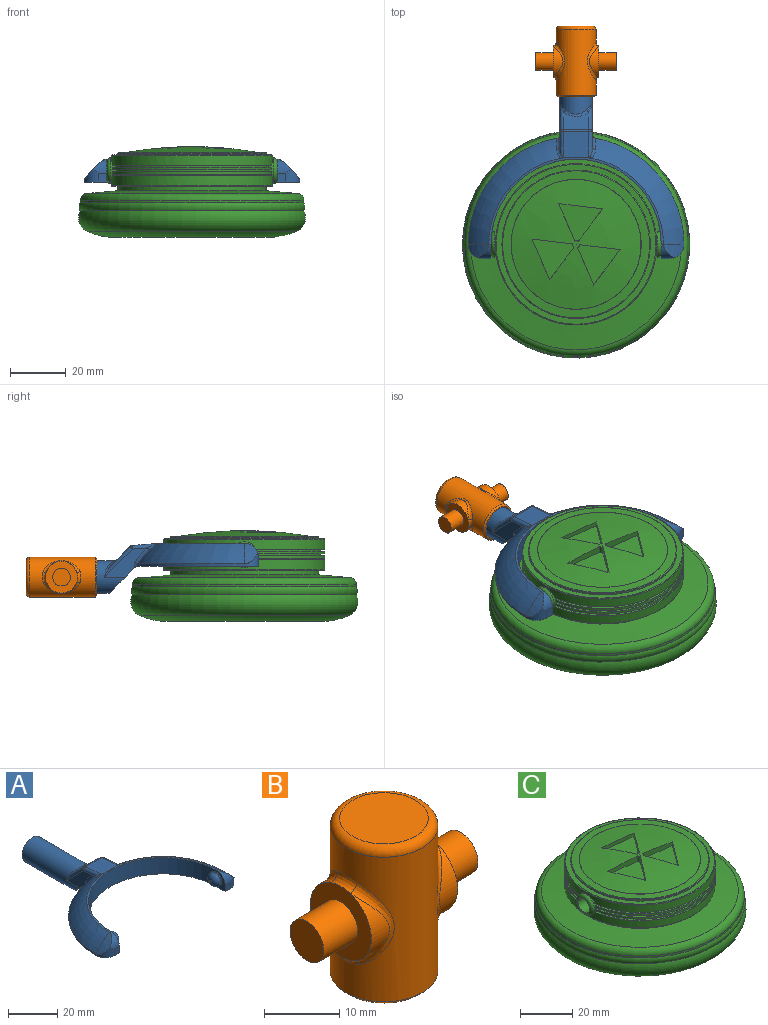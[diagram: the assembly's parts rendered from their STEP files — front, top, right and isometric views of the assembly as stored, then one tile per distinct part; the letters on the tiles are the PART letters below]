
ASSEMBLY  parts=3 mates=2
PART A: 48 faces, bbox 77.3x80.8x18.2 mm
  f0: plane 11.99x9.83mm, normal (0,-0.71,-0.71), area 141.5mm2, adj f1,f2,f9,f30,f43,f46
  f1: plane 15.39x10.49mm, normal (-1,0,0), area 63.5mm2, adj f0,f30,f32,f36,f46,f47
  f2: plane 15.39x10.49mm, normal (1,0,0), area 63.5mm2, adj f0,f30,f34,f39,f43,f44
  f3: plane 9.14x6.37mm, normal (0,0.71,0.71), area 67.6mm2, adj f35,f36,f39,f40
  f4: cylinder r=38.61mm len=37.99mm, axis (0,0,-1), area 42.6mm2, adj f6,f9,f17,f46,f47
  f5: torus R=19.3mm, axis (0,0,-1), area 507.8mm2, adj f10,f11,f12,f29,f42,f44
  f6: torus R=19.3mm, axis (0,0,-1), area 507.8mm2, adj f4,f11,f15,f28,f45,f47
  f7: cylinder r=30.48mm len=60.96mm, axis (0,0,-1), area 746.6mm2, adj f8,f9,f11,f14,f21,f24
  f8: plane 8.13x5.08mm, normal (-1,0,0), area 19.9mm2, adj f7,f9,f13,f19,f24
  f9: plane 77.22x43.73mm, normal (0,0,-1), area 956.2mm2, adj f0,f4,f7,f8,f10,f13,f14,f16
  f10: cylinder r=38.61mm len=37.99mm, axis (0,0,-1), area 42.6mm2, adj f5,f9,f20,f43,f44
  f11: plane 62.55x30.95mm, normal (0,0,1), area 75mm2, adj f5,f6,f7,f18,f19,f27
  f12: cylinder r=22.71mm len=7.33mm, axis (0,1,0), area 24.8mm2, adj f5,f19,f20
  f13: plane 3.05x3.05mm, normal (0,-1,0), area 9.3mm2, adj f8,f9,f19,f20
  f14: plane 8.13x5.08mm, normal (1,0,0), area 19.9mm2, adj f7,f9,f16,f18,f21
  f15: cylinder r=22.71mm len=7.33mm, axis (0,1,0), area 24.8mm2, adj f6,f17,f18
  f16: plane 3.05x3.05mm, normal (0,-1,0), area 9.3mm2, adj f9,f14,f17,f18
  f17: cylinder r=5.08mm len=5.08mm, axis (0,0,-1), area 21.9mm2, adj f4,f9,f15,f16,f18
  f18: cylinder r=5.08mm len=5.08mm, axis (-1,0,0), area 21.9mm2, adj f11,f14,f15,f16,f17
  f19: cylinder r=5.08mm len=5.08mm, axis (-1,0,0), area 21.9mm2, adj f8,f11,f12,f13,f20
  f20: cylinder r=5.08mm len=5.08mm, axis (0,0,-1), area 21.9mm2, adj f9,f10,f12,f13,f19
  f21: cylinder r=3.17mm len=6.35mm, axis (-1,0,0), area 12.7mm2, adj f7,f14,f23
  f22: plane 1.27x1.27mm, normal (1,0,0), area 1.3mm2, adj f23
  f23: torus R=0.64mm, axis (1,0,0), area 56.5mm2, adj f21,f22
  f24: cylinder r=3.17mm len=6.35mm, axis (1,0,0), area 12.7mm2, adj f7,f8,f26
  f25: plane 1.27x1.27mm, normal (-1,0,0), area 1.3mm2, adj f26
  f26: torus R=0.64mm, axis (-1,0,0), area 56.5mm2, adj f24,f25
  f27: plane 9.86x9.36mm, normal (0,0.09,1), area 85.6mm2, adj f11,f28,f29,f32,f34,f35,f42,f45
  f28: plane 1.04x0.17mm, normal (0,-1,0), area 0mm2, adj f6,f27,f45
  f29: plane 1.04x0.17mm, normal (0,-1,0), area 0mm2, adj f5,f27,f42
  f30: cylinder r=5.84mm len=33.01mm, axis (0,-1,0), area 1029.7mm2, adj f0,f1,f2,f31,f38,f40,f41
  f31: plane 11.68x11.68mm, normal (0,1,0), area 107.2mm2, adj f30
  f32: cylinder r=1.27mm len=9.13mm, axis (0,-1,0.09), area 14.4mm2, adj f1,f27,f33,f45
  f33: sphere r=1.27mm, area 1.5mm2, adj f32,f35,f36
  f34: cylinder r=1.27mm len=9.13mm, axis (0,1,-0.09), area 14.4mm2, adj f2,f27,f37,f42
  f35: cylinder r=1.27mm len=9.14mm, axis (-1,0,0), area 8.1mm2, adj f3,f27,f33,f37
  f36: cylinder r=1.27mm len=10.91mm, axis (0,-0.71,0.71), area 23.1mm2, adj f1,f3,f33,f38
  f37: sphere r=1.27mm, area 1.5mm2, adj f34,f35,f39
  f38: bspline ~4.55x2.75mm, area 2.3mm2, adj f30,f36,f40
  f39: cylinder r=1.27mm len=10.91mm, axis (0,0.71,-0.71), area 23.1mm2, adj f2,f3,f37,f41
  f40: bspline ~9.14x2.56mm, area 10.7mm2, adj f3,f30,f38,f41
  f41: bspline ~5.23x3.53mm, area 2.3mm2, adj f30,f39,f40
  f42: bspline ~4.62x3.14mm, area 5.2mm2, adj f5,f27,f29,f34,f44
  f43: cylinder r=1.27mm len=1.74mm, axis (0,0,-1), area 1.9mm2, adj f0,f2,f9,f10,f44
  f44: bspline ~8.6x7.86mm, area 11.9mm2, adj f2,f5,f10,f42,f43
  f45: bspline ~4.62x3.14mm, area 5.2mm2, adj f6,f27,f28,f32,f47
  f46: cylinder r=1.27mm len=1.74mm, axis (0,0,-1), area 1.9mm2, adj f0,f1,f4,f9,f47
  f47: bspline ~8.6x7.86mm, area 11.9mm2, adj f1,f4,f6,f45,f46
PART B: 25 faces, bbox 28.9x15.5x25.4 mm
  f0: cylinder r=5.71mm len=10.81mm, axis (-1,0,0), area 26.2mm2, adj f5,f15
  f1: cylinder r=5.71mm len=10.81mm, axis (-1,0,0), area 26.2mm2, adj f8,f11
  f2: cylinder r=7.14mm len=23.5mm, axis (0,0,-1), area 763.2mm2, adj f9,f10,f11,f12,f13,f14,f15,f16
  f3: plane 11.75x11.75mm, normal (0,0,1), area 108.4mm2, adj f17
  f4: plane 13.02x13.02mm, normal (0,0,-1), area 16.3mm2, adj f22,f24
  f5: plane 11.46x11.46mm, normal (1,0,0), area 70.9mm2, adj f0,f6,f13,f16,f18
  f6: cylinder r=5.71mm len=10.81mm, axis (-1,0,0), area 26.2mm2, adj f5,f14
  f7: cylinder r=5.71mm len=10.81mm, axis (-1,0,0), area 26.2mm2, adj f8,f10
  f8: plane 11.46x11.46mm, normal (-1,0,0), area 70.9mm2, adj f1,f7,f9,f12,f20
  f9: bspline ~4.64x1.73mm, area 6.5mm2, adj f2,f8,f10,f11
  f10: bspline ~13.62x4.91mm, area 20.7mm2, adj f2,f7,f9,f12
  f11: bspline ~13.6x4.87mm, area 20.7mm2, adj f1,f2,f9,f12
  f12: bspline ~4.64x1.73mm, area 6.5mm2, adj f2,f8,f10,f11
  f13: bspline ~4.64x1.73mm, area 6.5mm2, adj f2,f5,f14,f15
  f14: bspline ~13.62x4.91mm, area 20.7mm2, adj f2,f6,f13,f16
  f15: bspline ~13.6x4.87mm, area 20.7mm2, adj f0,f2,f13,f16
  f16: bspline ~4.64x1.73mm, area 6.5mm2, adj f2,f5,f14,f15
  f17: torus R=5.87mm, axis (0,0,1), area 83.8mm2, adj f2,f3
  f18: cylinder r=3.17mm len=6.35mm, axis (-1,0,0), area 126.7mm2, adj f5,f19
  f19: plane 6.35x6.35mm, normal (1,0,0), area 31.7mm2, adj f18
  f20: cylinder r=3.17mm len=6.35mm, axis (1,0,0), area 126.7mm2, adj f8,f21
  f21: plane 6.35x6.35mm, normal (-1,0,0), area 31.7mm2, adj f20
  f22: cylinder r=6.1mm len=22.86mm, axis (0,0,-1), area 875.6mm2, adj f4,f23
  f23: plane 12.19x12.19mm, normal (0,0,-1), area 116.7mm2, adj f22
  f24: cone r=7.14mm half-angle=45deg, axis (0,0,1), area 38.5mm2, adj f2,f4
PART C: 64 faces, bbox 96.3x96.3x32.5 mm
  f0: cylinder r=28.87mm len=57.73mm, axis (0,0,-1), area 628.4mm2, adj f1,f2,f54,f55,f60
  f1: plane 57.14x24.71mm, normal (0,0,1), area 101.4mm2, adj f0,f3,f54,f55
  f2: plane 57.14x24.71mm, normal (0,0,1), area 101.4mm2, adj f0,f4,f54,f55
  f3: cylinder r=27.61mm len=54.58mm, axis (0,0,-1), area 50.1mm2, adj f1,f6,f54,f55
  f4: cylinder r=27.61mm len=54.58mm, axis (0,0,-1), area 50.1mm2, adj f2,f5,f54,f55
  f5: plane 57.17x24.53mm, normal (0,0,-1), area 100.8mm2, adj f4,f8,f54,f55
  f6: plane 57.17x24.53mm, normal (0,0,-1), area 100.8mm2, adj f3,f7,f54,f55
  f7: cylinder r=28.87mm len=57.06mm, axis (0,0,-1), area 76.2mm2, adj f6,f9,f54,f55
  f8: cylinder r=28.87mm len=57.06mm, axis (0,0,-1), area 76.2mm2, adj f5,f10,f54,f55
  f9: plane 57.02x24.31mm, normal (0,0,1), area 100.4mm2, adj f7,f11,f54,f55
  f10: plane 57.02x24.31mm, normal (0,0,1), area 100.4mm2, adj f8,f12,f54,f55
  f11: cylinder r=27.61mm len=54.45mm, axis (0,0,-1), area 48.1mm2, adj f9,f13,f54,f55
  f12: cylinder r=27.61mm len=54.45mm, axis (0,0,-1), area 48.1mm2, adj f10,f14,f54,f55
  f13: plane 57.12x24.36mm, normal (0,0,-1), area 100.4mm2, adj f11,f15,f54,f55
  f14: plane 57.12x24.36mm, normal (0,0,-1), area 100.4mm2, adj f12,f16,f54,f55
  f15: cylinder r=28.87mm len=57.06mm, axis (0,0,-1), area 79.3mm2, adj f13,f22,f54,f55
  f16: cylinder r=28.87mm len=57.06mm, axis (0,0,-1), area 79.3mm2, adj f14,f21,f54,f55
  f17: cylinder r=27.61mm len=54.58mm, axis (0,0,-1), area 50.1mm2, adj f19,f22,f54,f55
  f18: cylinder r=27.61mm len=54.58mm, axis (0,0,-1), area 50.1mm2, adj f20,f21,f54,f55
  f19: plane 57.24x24.77mm, normal (0,0,-1), area 101.4mm2, adj f17,f23,f54,f55
  f20: plane 57.24x24.77mm, normal (0,0,-1), area 101.4mm2, adj f18,f23,f54,f55
  f21: plane 57.07x24.48mm, normal (0,0,1), area 100.8mm2, adj f16,f18,f54,f55
  f22: plane 57.07x24.48mm, normal (0,0,1), area 100.8mm2, adj f15,f17,f54,f55
  f23: cylinder r=28.87mm len=57.73mm, axis (0,0,-1), area 595.8mm2, adj f19,f20,f54,f55,f61
  f24: sphere r=135.39mm, area 1385.3mm2, adj f38,f39,f40,f41,f43,f44,f45,f46
  f25: plane 39.33x39.33mm, normal (0,0,-1), area 1214.6mm2, adj f26
  f26: torus R=20.12mm, axis (0,0,-1), area 1429.3mm2, adj f25,f27
  f27: torus R=27.74mm, axis (0,0,-1), area 3542.1mm2, adj f26,f28
  f28: torus R=35.36mm, axis (0,0,-1), area 2180.1mm2, adj f27,f29
  f29: torus R=37.64mm, axis (0,0,-1), area 740.9mm2, adj f28,f30
  f30: cylinder r=40.06mm len=80.11mm, axis (0,0,-1), area 213.3mm2, adj f29,f34
  f31: cone r=26.57mm half-angle=85deg, axis (0,0,-1), area 2265mm2, adj f32,f34
  f32: cylinder r=26.57mm len=53.14mm, axis (0,0,-1), area 265mm2, adj f31,f33
  f33: plane 57.23x57.23mm, normal (0,0,-1), area 354.5mm2, adj f32,f60
  f34: torus R=37.52mm, axis (0,0,1), area 928.6mm2, adj f30,f31
  f35: cone r=26.57mm half-angle=87deg, axis (0,0,-1), area 475.4mm2, adj f62,f63
  f36: cylinder r=26.57mm len=53.14mm, axis (0,0,-1), area 92.3mm2, adj f37,f62
  f37: plane 57.23x57.23mm, normal (0,0,1), area 354.5mm2, adj f36,f61
  f38: plane 13.42x5.76mm, normal (0.92,0.39,0), area 32.2mm2, adj f24,f39,f41,f42
  f39: cylinder r=1.27mm len=2.53mm, axis (0,0,1), area 3.4mm2, adj f24,f38,f40,f42
  f40: plane 11.7x8.74mm, normal (-0.8,0.6,0), area 32.2mm2, adj f24,f39,f41,f42
  f41: plane 15.76x1.87mm, normal (-0.12,-0.99,0), area 28mm2, adj f24,f38,f40,f42
  f42: plane 15.76x13.57mm, normal (0,0,1), area 108.3mm2, adj f38,f39,f40,f41
  f43: plane 14.5x2.53mm, normal (-0.12,-0.99,0), area 32.2mm2, adj f24,f44,f46,f47
  f44: cylinder r=1.27mm len=2.53mm, axis (0,0,1), area 3.4mm2, adj f24,f43,f45,f47
  f45: plane 13.42x5.76mm, normal (0.92,0.39,0), area 32.2mm2, adj f24,f44,f46,f47
  f46: plane 12.72x9.5mm, normal (-0.8,0.6,0), area 28mm2, adj f24,f43,f45,f47
  f47: plane 15.26x14.44mm, normal (0,0,1), area 108.3mm2, adj f43,f44,f45,f46
  f48: cylinder r=1.27mm len=2.53mm, axis (0,0,1), area 3.4mm2, adj f24,f49,f51,f52
  f49: plane 14.5x2.53mm, normal (-0.12,-0.99,0), area 32.2mm2, adj f24,f48,f50,f52
  f50: plane 14.59x6.26mm, normal (0.92,0.39,0), area 28mm2, adj f24,f49,f51,f52
  f51: plane 11.7x8.74mm, normal (-0.8,0.6,0), area 32.2mm2, adj f24,f48,f50,f52
  f52: plane 15x14.59mm, normal (0,0,1), area 108.3mm2, adj f48,f49,f50,f51
  f53: plane 6.6x6.6mm, normal (1,0,0), area 2.6mm2, adj f58,f59
  f54: cylinder r=4.57mm len=9.14mm, axis (-1,0,0), area 23.9mm2, adj f0,f1,f2,f3,f4,f5,f6,f7
  f55: cylinder r=4.57mm len=9.14mm, axis (-1,0,0), area 22.3mm2, adj f0,f1,f2,f3,f4,f5,f6,f7
  f56: plane 6.6x6.6mm, normal (-1,0,0), area 2.6mm2, adj f57,f59
  f57: torus R=3.3mm, axis (1,0,0), area 51.5mm2, adj f55,f56
  f58: torus R=3.3mm, axis (1,0,0), area 51.5mm2, adj f53,f54
  f59: cylinder r=3.17mm len=60.96mm, axis (1,0,0), area 1216.1mm2, adj f53,f56
  f60: torus R=28.61mm, axis (0,0,1), area 72.1mm2, adj f0,f33
  f61: torus R=28.61mm, axis (0,0,-1), area 72.1mm2, adj f23,f37
  f62: torus R=26.31mm, axis (0,0,1), area 64.2mm2, adj f35,f36
  f63: torus R=23.29mm, axis (0,0,1), area 4.5mm2, adj f24,f35
PLACE A t=(32.34,27.52,20.85)mm
PLACE B rot(axis=(-1,0,0),90deg) t=(32.34,80.3,16.88)mm
PLACE C t=(32.34,27.52,33.52)mm
MATE revolute A.f24 <-> C.f54  axis (-1,0,0) through (62.82,27.52,24.92)mm
MATE revolute B.f2 <-> A.f30  axis (0,-1,0) through (32.34,103.16,16.88)mm
